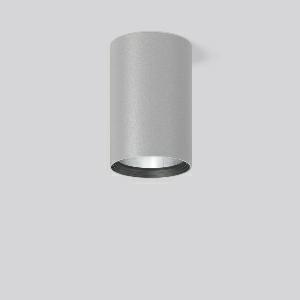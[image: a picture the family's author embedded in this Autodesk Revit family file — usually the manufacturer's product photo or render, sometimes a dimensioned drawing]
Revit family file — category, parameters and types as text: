
# Revit family: heledon_maxi_a_931244_004_2_af57
name_source: partatom
category: Lighting Fixtures
units: mm (PartAtom-declared; Revit-internal decimal feet)

## family parameters
Cut with Voids When Loaded = No
Host = Face
Light Source = No
Part Type = Normal
Room Calculation Point = No
Round Connector Dimension = Use Diameter
Shared = No

## types (1)
- HELEDON maxi A (1 x LED Modul 927 bakery, 3300 lm, 2700)
    Apparent Load = 33 VA
    Approval mark = CE
    CIE Flux Codes = 100 100 100 100 100
    Color Rendering = 90
    Color Temperature = 2700
    Default Elevation = 1800 mm
    Description = Series: HELEDON maxi
Cylindrical surface-mounted downlight. Housing: die-cast aluminium, powder-coated. Internal ceiling frame polycarbonate with bayonet mounting. Black plastic ring and recessed LED to prevent glare from the side. Optical assembly with reflector made of MIRO-Silver with 98% total light reflection for outstanding efficiency - can be changed without tools. Special LED for illumination of pastries included. Suitable for Ceiling mounting. Easy installation with a separate ceiling frame with bayonet mounting and plug connection. Driver integrated. Connected via plug-in connector. High quality converter without flickering and stroboscopic effect. The following accessories can be mounted without use of tools: interchangeable lenses, decorative glasses, honeycomb louvre, clear and frosted diffusers, white interchangeable plastic ring. 
Colour: silver
Diameter: 123 mm
Height: 183 mm
Lamp: LED
Socket: without socket
Colour temperature: bakery
Colour rendering index (CRI): 97
System power: 33 W
Rated luminous flux: 3300 lm
Luminous efficiency: 100 lm/W
Control gear: Regulated power supply
Protection class: I
Type of protection: IP 20
    Height = 183 mm
    Lamp = 1 x LED Modul 927 bakery
    Lamp Light Flux = 3300 lm
    Lamp count = 1
    Length = 123 mm
    Lifetime = 50000 h
    Luminous efficacy = 100 lm/W
    Manufacturer = RZB
    ModVariant = No
    Model = 931244.004.2
    Mounting Place = Ceiling
    Mounting Type = Surface mounted
    Number of Poles = 1
    OnlyDefault = Yes
    Power Factor = 1
    Product Name = HELEDON maxi A
    Product group = Surface mounted downlights
    ProductGroupID = 302
    Protection Class = Protection class I
    Protection Degree = IP 20
    RLX_Detail_Level = 1
    RLX_Emergency_Light_Flux = 0 lm
    RLX_Emergency_Type = 0
    RLX_Emergency_Type_DB = No
    RlxData = <blob elided: 96785 chars, md5=6a974174>
    Socket = socket
    Standby Power = 0 W
    System Light Flux = 3300 lm
    System Power = 33 W
    Type Comments = Product without accessories
    Type Image = 931192.004.jpg
    URL = http://relux.com
    VarID = ---
    Voltage = 230 V
    Voltage Range = 220-240 V
    Weight = 0.00 kg
    Width = 0 mm  [stored 0 ft]

note: [stored X ft] marks values corroborated as IEEE doubles in the binary element streams (Revit-internal decimal feet)

## geometry (parser evidence)
native form markers: Blend x4, Sweep x11
no freeform markers — native parametric forms only
